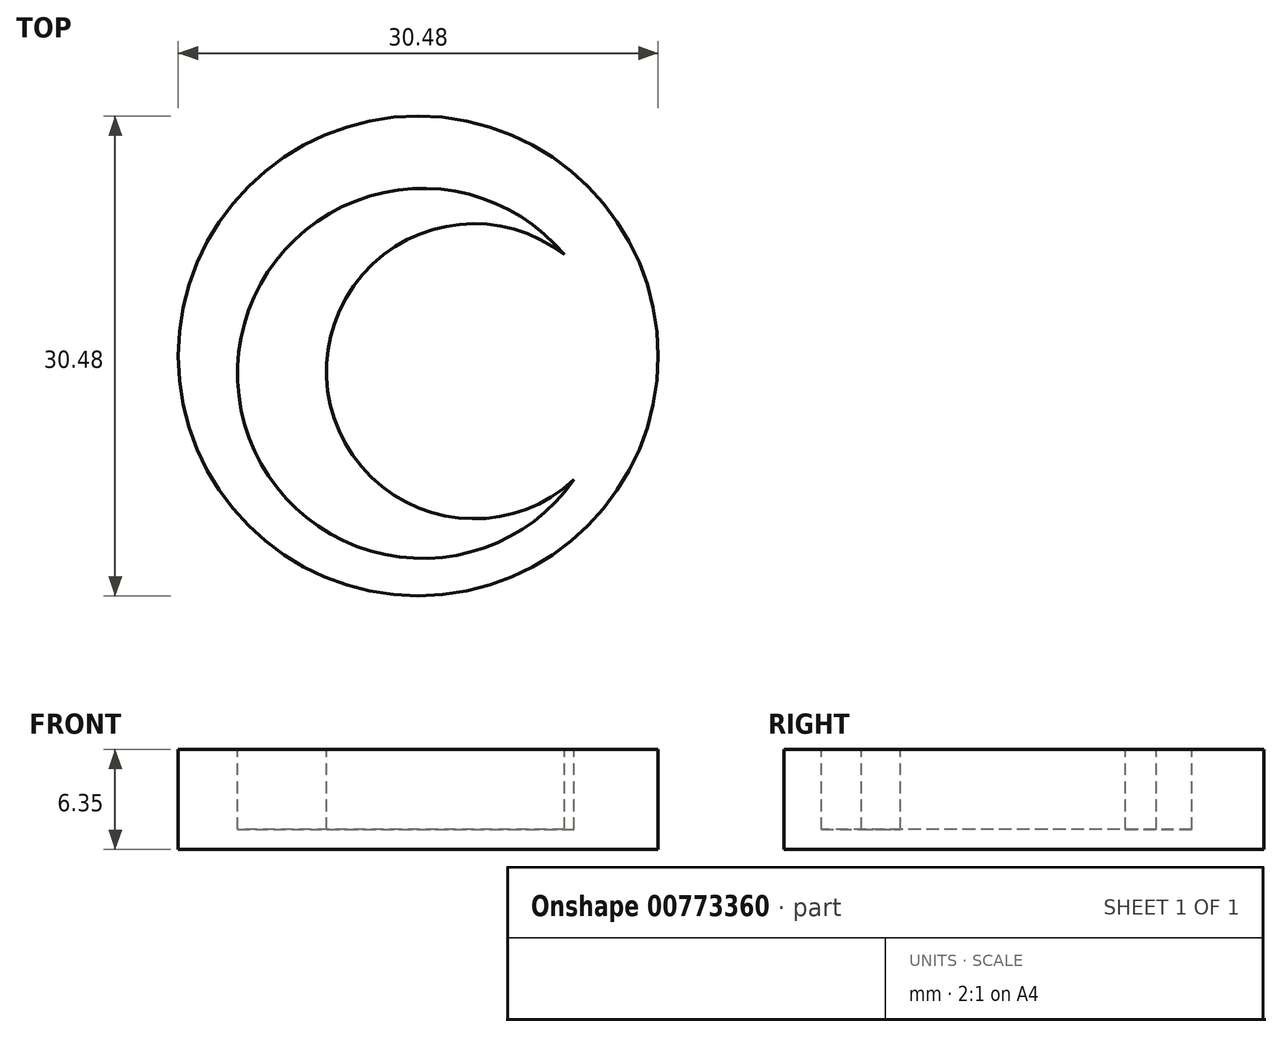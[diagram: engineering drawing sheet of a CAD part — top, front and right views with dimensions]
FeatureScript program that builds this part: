
annotation { "Feature Type Name" : "Feature", "Feature Type Description" : "" }
export const myFeature = defineFeature(function(context is Context, id is Id, definition is map)
    precondition{}
    {
        {
            var Q0;
            Q0=qCreatedBy(makeId("Top.planeOp"),FACE);
            var sketch = newSketch(context, id + "F0", { "sketchPlane" : qUnion([Q0])});
            skCircle(sketch, "E0", {"center": v(0, 0) * mm, "radius": 15.24 * mm});
            skSolve(sketch);
        }
        {
            var Q0;
            Q0 = qSketchRegion(id + "F0", true);
            extrude(context, id + "F1", {"entities" : qUnion([Q0]), "depth" : 6.35 * mm, "offsetDistance" : 25.4 * mm});
        }
        {
            var Q0;
            Q0=makeQuery(id+"F1.opExtrude","CAP_FACE",FACE,{"disambiguationData":[OSD([sQuery(id+"F0.wireOp",EDGE,"E0")])],"isStart":false});
            var sketch = newSketch(context, id + "F2", { "sketchPlane" : qUnion([Q0])});
            skArc(sketch, "E1", {"start": v(9.3, 6.43) * mm, "mid": v(-5.82, -1.36) * mm, "end": v(9.9, -7.85) * mm});
            skArc(sketch, "E2", {"start": v(9.3, 6.43) * mm, "mid": v(-11.46, -1.6) * mm, "end": v(9.9, -7.85) * mm});
            skSolve(sketch);
        }
        {
            var Q0;
            Q0 = qSketchRegion(id + "F2", true);
            extrude(context, id + "F3", {"entities" : qUnion([Q0]), "operationType" : NewBodyOperationType.REMOVE, "oppositeDirection" : true, "depth" : 5.08 * mm, "offsetDistance" : 25.4 * mm});
        }
    });
